# Revit family: IS_Active_B8066_BIM_DE
name_source: partatom
category: Plumbing Fixtures
revit_build: Autodesk Revit MEP 2016 (Build: 20161004_0715(x64)
units: mm (PartAtom-declared; Revit-internal decimal feet)

## family parameters
Always vertical = No
Cut with Voids When Loaded = No
OmniClass Number = 23.45.55.17
OmniClass Title = Mixing Faucets
Part Type = Normal
Room Calculation Point = No
Round Connector Dimension = Use Diameter
Shared = No
Work Plane-Based = No

## types (1)
- B8066AA - ACTIVE exposed shower single lever mixer
    Accessories = www.idealstandard.de\ersatzteile
    AssetType = Fixed
    BIMObjectName = ISI_IdealStandard_ShowerThermostaticvalves_ACTIVE_B8066AA
    BIMobject category = Taps & Mixers
    BOSUseNativeGeometries = 1
    BarCode = 3800861001416
    Brand = Ideal Standard
    Brand url = http://www.idealstandard.de
    CodePerformance = EN 817, DIN 4109, Gruppe 1
    Color = Chrome
    ConnectionType = Plumbing
    Cost = 0 $
    CurrencyUnit = €
    CurrentRevision = 1
    Description = B8066AA ACTIVE exposed shower single lever mixer
    DurationUnit = Jaar
    EAN code = https://3800861001416
    Edition number = 1
    ExpectedLife = 25
    FaucetFunction = mixed
    FaucetOperation = leverhandle
    FaucetType = pillar
    Features = ACTIVE exposed shower single lever mixer
    Finish = Chrome
    IFC Classification = Sanitary Terminal
    IfcExportAs = Sanitary terminal type
    IfcExportType = BRASSWARE SHOWER
    Installation instructions = http://www.idealstandard.de
    InstallationInstructions = www.idealstandard.de\produkte
    LinearUnits = millimetres
    MainColor = Chrome
    MaintenanceInformation = www.idealstandard.de
    Manufacturer = http://www.idealstandard.de
    Manufacturer name = Ideal Standard
    ManufacturerURL = http://www.idealstandard.de
    Material = Brass
    Material main = Brass
    Model = B8066AA
    ModelNumber = B8066AA
    ModelReference = B8066AA ACTIVE exposed shower single lever mixer
    NBS Reference Code = 35-06-82
    NBS Reference Description = Shower Mixers
    Name = ISI_IdealStandard_ShowerThermostaticvalves_ACTIVE_B8066AA
    NettWeight = 2,783 kg
    Nominal height = 0
    Nominal width = 0
    NominalHeight = 116 mm
    NominalLength = 122 mm
    NominalWidth = 275 mm
    OmniClass Code = 23-31 11 00
    OmniClass Description = Faucets
    Product Guid = 1a05a93a-61bd-432c-a8d2-7f0910bb3770
    Product SKU = B8066
    Product certification = EN 817, DIN 4109, Gruppe 1
    Product data url = https://bimobject.com
    Product family = ACTIVE
    Product group = Shower Mixer
    Product name = ACTIVE exposed shower single lever mixer
    Product url = http://www.idealstandard.de
    ProductInformation = www.idealstandard.de/produkte
    QR code = http://bimobject.com
    Shape = Sculptured
    Size = 116 x 122 x 275mm
    Space = Internal
    SpareParts = www.idealstandard.de/ersatzteile
    Technical description = http://www.idealstandard.de
    TestPressure = 10 Bar
    URL = http://www.idealstandard.de
    Uniclass 1.4 Code = L8212
    Uniclass 1.4 Description = Fittings
    Uniclass 2.0 Code = PR-35-06-82
    Uniclass 2.0 Description = Shower Mixers
    Uniclass 2015 Code = Pr_40_20_87_78
    Uniclass 2015 Name = Shower manual water supply sets
    Uniclass2015Code = Pr_40_20_87_80
    Uniclass2015Title = Shower thermostatic valves
    Uniclass2015Version = Products v1.1
    ValveMechanism = ceramic disc
    ValveOperation = lever
    VolumeUnits = Litres
    Weight Net (Kg) = 2.78
    WorkingPressure = 1-5 Bar

## geometry (parser evidence)
native form markers: Blend x2, Sweep x3
no freeform markers — native parametric forms only
